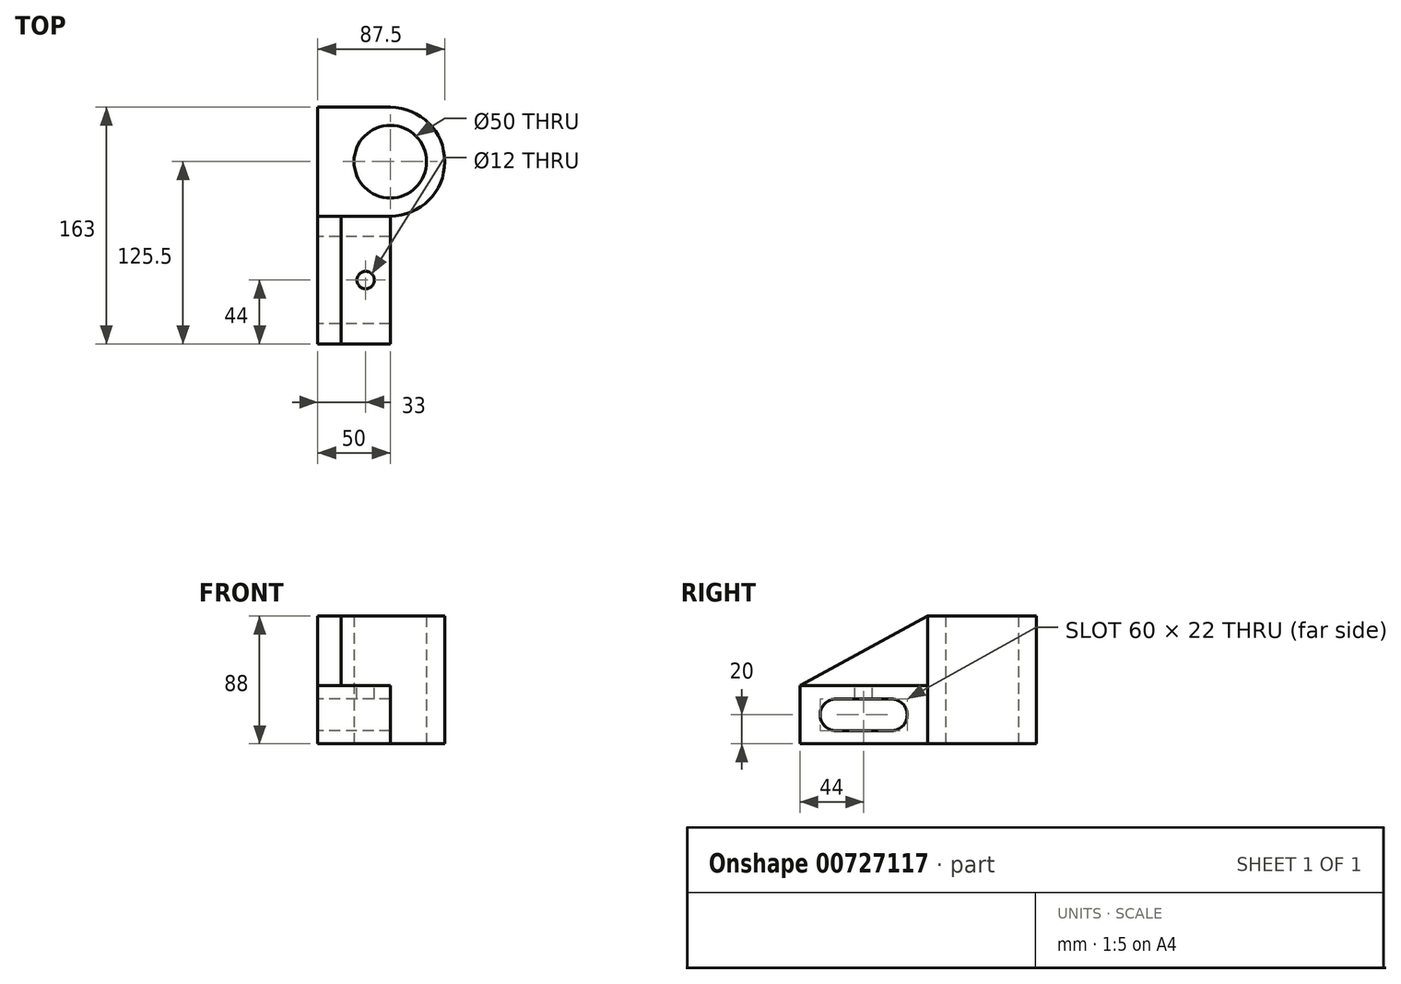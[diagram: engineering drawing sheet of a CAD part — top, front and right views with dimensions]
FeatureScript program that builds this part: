
annotation { "Feature Type Name" : "Feature", "Feature Type Description" : "" }
export const myFeature = defineFeature(function(context is Context, id is Id, definition is map)
    precondition{}
    {
        {
            var Q0;
            Q0=qCreatedBy(makeId("Top.planeOp"),FACE);
            var sketch = newSketch(context, id + "F0", { "sketchPlane" : qUnion([Q0])});
            skLineSegment(sketch, "E0.bottom", {"start": v(0, 0) * mm, "end": v(50, 0) * mm});
            skLineSegment(sketch, "E0.top", {"start": v(0, 75) * mm, "end": v(50, 75) * mm});
            skLineSegment(sketch, "E0.left", {"start": v(0, 0) * mm, "end": v(0, 75) * mm});
            skCircle(sketch, "E1", {"center": v(50, 37.5) * mm, "radius": 25 * mm});
            skArc(sketch, "E2", {"start": v(50, 0) * mm, "mid": v(87.5, 37.5) * mm, "end": v(50, 75) * mm});
            skSolve(sketch);
        }
        {
            var Q0;
            Q0 = qSketchRegion(id + "F0", true);
            extrude(context, id + "F1", {"entities" : qUnion([Q0]), "depth" : 88 * mm, "offsetDistance" : 25 * mm});
        }
        {
            var Q0;
            Q0=qCreatedBy(makeId("Right.planeOp"),FACE);
            var sketch = newSketch(context, id + "F2", { "sketchPlane" : qUnion([Q0])});
            skLineSegment(sketch, "E3.bottom", {"start": v(0, 0) * mm, "end": v(-88, 0) * mm});
            skLineSegment(sketch, "E3.top", {"start": v(0, 40) * mm, "end": v(-88, 40) * mm});
            skLineSegment(sketch, "E3.left", {"start": v(0, 0) * mm, "end": v(0, 40) * mm});
            skLineSegment(sketch, "E3.right", {"start": v(-88, 0) * mm, "end": v(-88, 40) * mm});
            skLineSegment(sketch, "E4", {"start": v(0, 0) * mm, "end": v(0, 20) * mm});
            skArc(sketch, "E5", {"start": v(-25, 9) * mm, "mid": v(-14, 20) * mm, "end": v(-25, 31) * mm});
            skLineSegment(sketch, "E6", {"start": v(-88, 0) * mm, "end": v(-88, 20) * mm});
            skArc(sketch, "E7", {"start": v(-63, 31) * mm, "mid": v(-74, 20) * mm, "end": v(-63, 9) * mm});
            skLineSegment(sketch, "E8", {"start": v(-63, 31) * mm, "end": v(-25, 31) * mm});
            skLineSegment(sketch, "E9", {"start": v(-63, 9) * mm, "end": v(-25, 9) * mm});
            skSolve(sketch);
        }
        {
            var Q0;
            Q0 = qSketchRegion(id + "F2", true);
            extrude(context, id + "F3", {"entities" : qUnion([Q0]), "operationType" : NewBodyOperationType.ADD, "depth" : 50 * mm, "offsetDistance" : 25 * mm});
        }
        {
            var Q0;
            Q0=qCreatedBy(makeId("Right.planeOp"),FACE);
            var sketch = newSketch(context, id + "F4", { "sketchPlane" : qUnion([Q0])});
            skLineSegment(sketch, "E10", {"start": v(0, 40) * mm, "end": v(0, 88) * mm});
            skLineSegment(sketch, "E11", {"start": v(0, 40) * mm, "end": v(-88, 40) * mm});
            skLineSegment(sketch, "E12", {"start": v(-88, 40) * mm, "end": v(0, 88) * mm});
            skSolve(sketch);
        }
        {
            var Q0;
            Q0 = qSketchRegion(id + "F4", true);
            extrude(context, id + "F5", {"entities" : qUnion([Q0]), "operationType" : NewBodyOperationType.ADD, "depth" : 16 * mm, "offsetDistance" : 25 * mm});
        }
        {
            var Q0;
            Q0=makeQuery(id+"F3.opExtrude","SWEPT_FACE",FACE,{"disambiguationData":[OSD([sQuery(id+"F2.wireOp",EDGE,"E3.top")])]});
            var sketch = newSketch(context, id + "F6", { "sketchPlane" : qUnion([Q0])});
            skPoint(sketch, "E13.endSnap0", {"position": v(50, -44) * mm});
            skCircle(sketch, "E14", {"center": v(33, -44) * mm, "radius": 6 * mm});
            skSolve(sketch);
        }
        {
            var Q0;
            Q0 = qSketchRegion(id + "F6", true);
            extrude(context, id + "F7", {"entities" : qUnion([Q0]), "operationType" : NewBodyOperationType.REMOVE, "endBound" : BoundingType.UP_TO_NEXT, "oppositeDirection" : true, "depth" : 25 * mm, "offsetDistance" : 25 * mm});
        }
    });
